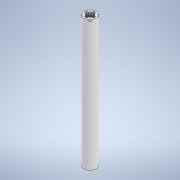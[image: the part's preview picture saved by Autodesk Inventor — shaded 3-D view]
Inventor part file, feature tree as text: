
AUTODESK INVENTOR PART (.ipt)
format: ipt  version: 2022 (Build 260153000, 153)  size: 205,824 bytes
history: native  units: in
note: dims shown in document units (in); Inventor stores cm internally (conversion verified against a paired STEP export)
features: extrude x5, sketch x4
ambient origin geometry x8: Origin, YZ Plane, XZ Plane, XY Plane, X Axis, Y Axis, Z Axis, Center Point
bodies: Solid1 (feature_tree)
feature tree (9):
  extrude  "Extrusion1"  Depth=6.2205in TaperAngle=0.0deg
  extrude  "Extrusion2"  Depth=0.7087in
  extrude  "Extrusion3"  Depth=0.315in TaperAngle=0.0deg
  extrude  "Extrusion5"  Depth=0.0394in
  extrude  "Extrusion6"  Depth=0.0394in
  sketch  "Sketch1"  dims[d0=0.5512in d1=6.2205in d2=0.0in]
  sketch  "Sketch3"  dims[d13=0.0in d14=0.0in d15=0.7087in]
  sketch  "Sketch5"  dims[d19=0.3543in d20=0.315in d21=0.0in]
  sketch  "Sketch6"  dims[d36=0.0394in d37=0.0394in d38=0.0394in d39=0.0394in d52=1.5748in d54=360.0deg d56=1.1811in d57=0.0in d58=0.2953in d59=0.1181in d60=0.1181in d61=0.1181in d62=0.1181in d63=0.1181in d64=0.1181in d65=0.1181in d66=0.1181in d69=0.0787in d70=0.1949in d71=0.1949in d72=1.5748in d74=360.0deg d76=0.0787in d77=0.0in d67=0.0197in d68=0.0344in]
